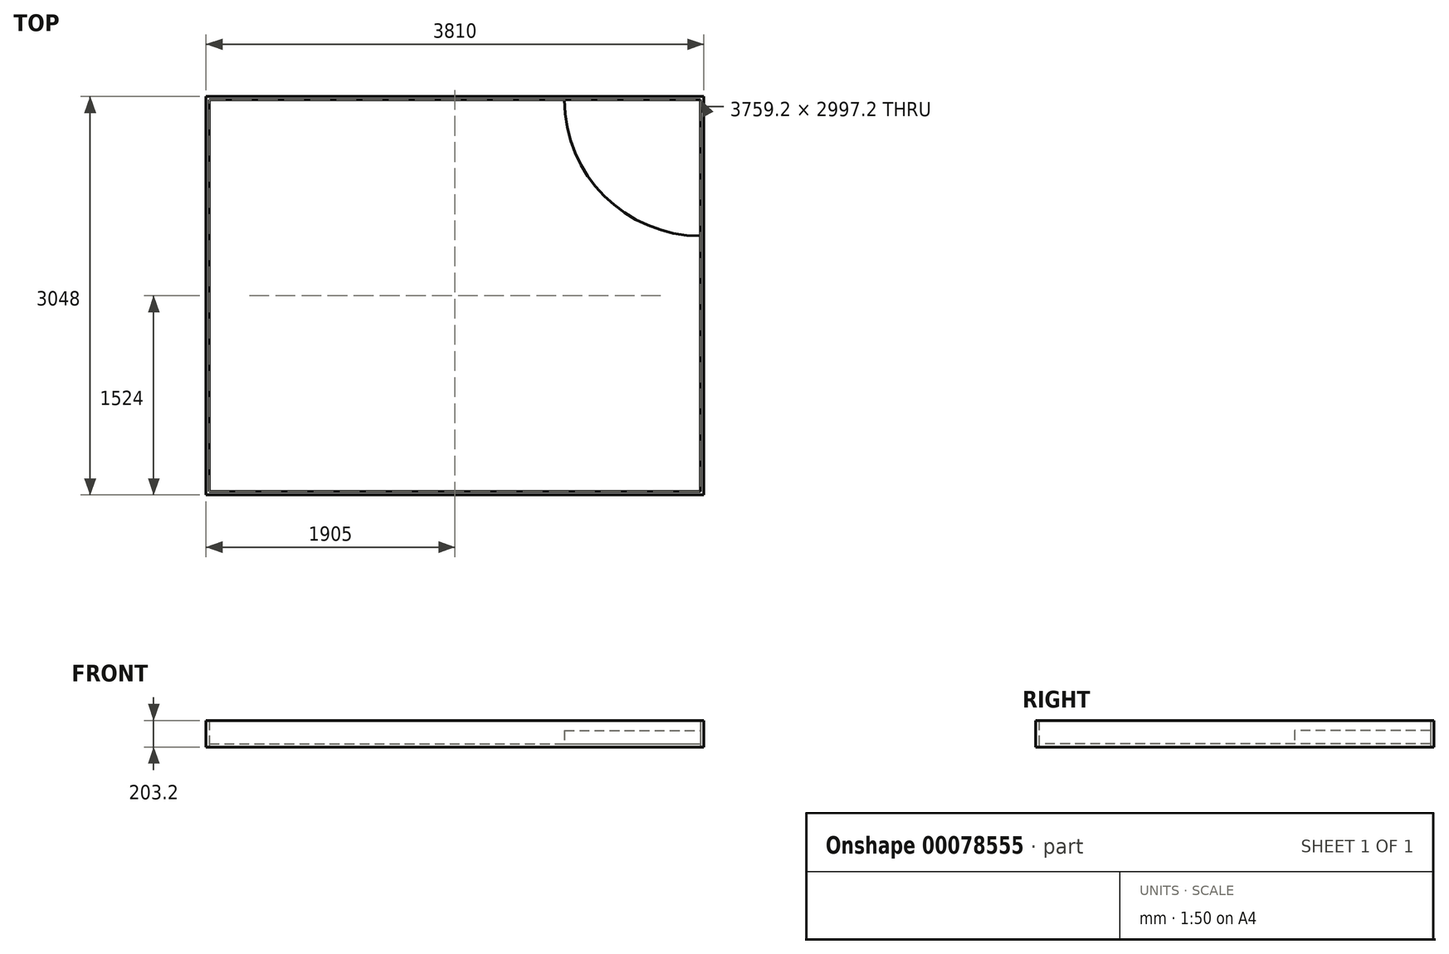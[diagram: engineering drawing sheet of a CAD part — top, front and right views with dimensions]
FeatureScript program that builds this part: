
annotation { "Feature Type Name" : "Feature", "Feature Type Description" : "" }
export const myFeature = defineFeature(function(context is Context, id is Id, definition is map)
    precondition{}
    {
        {
            var Q0;
            Q0=qCreatedBy(makeId("Top.planeOp"),FACE);
            var sketch = newSketch(context, id + "F0", { "sketchPlane" : qUnion([Q0])});
            skLineSegment(sketch, "E0.bottom", {"start": v(-1874.04, 1728.23) * mm, "end": v(1885.16, 1728.23) * mm});
            skLineSegment(sketch, "E0.top", {"start": v(-1874.04, -1268.97) * mm, "end": v(1885.16, -1268.97) * mm});
            skLineSegment(sketch, "E0.left", {"start": v(-1874.04, 1728.23) * mm, "end": v(-1874.04, -1268.97) * mm});
            skLineSegment(sketch, "E0.right", {"start": v(1885.16, 1728.23) * mm, "end": v(1885.16, -1268.97) * mm});
            skSolve(sketch);
        }
        {
            var Q0;
            Q0=makeQuery(id+"F0.imprint","IMPRINT",FACE,{"disambiguationData":[TD([[makeQuery(id+"F0.imprint","IMPRINT",EDGE,{"derivedFrom":sQuery(id+"F0.wireOp",EDGE,"E0.bottom")}),-1.0]])]});
            extrude(context, id + "F1", {"entities" : qUnion([Q0]), "depth" : 25.4 * mm});
        }
        {
            var Q0;
            Q0=makeQuery(id+"F1.opExtrude","CAP_FACE",FACE,{"disambiguationData":[OSD([sQuery(id+"F0.wireOp",EDGE,"E0.bottom"),sQuery(id+"F0.wireOp",EDGE,"E0.top"),sQuery(id+"F0.wireOp",EDGE,"E0.left"),sQuery(id+"F0.wireOp",EDGE,"E0.right")])],"isStart":true});
            var sketch = newSketch(context, id + "F2", { "sketchPlane" : qUnion([Q0])});
            skLineSegment(sketch, "E1.bottom", {"start": v(1910.56, -1753.63) * mm, "end": v(-1899.44, -1753.63) * mm});
            skLineSegment(sketch, "E1.top", {"start": v(1910.56, 1294.37) * mm, "end": v(-1899.44, 1294.37) * mm});
            skLineSegment(sketch, "E1.left", {"start": v(1910.56, -1753.63) * mm, "end": v(1910.56, 1294.37) * mm});
            skLineSegment(sketch, "E1.right", {"start": v(-1899.44, -1753.63) * mm, "end": v(-1899.44, 1294.37) * mm});
            skSolve(sketch);
        }
        {
            var Q0;
            Q0=makeQuery(id+"F2.imprint","IMPRINT",FACE,{"disambiguationData":[TD([[makeQuery(id+"F2.imprint","IMPRINT",EDGE,{"derivedFrom":sQuery(id+"F2.wireOp",EDGE,"E1.bottom")}),-1.0]])]});
            extrude(context, id + "F3", {"entities" : qUnion([Q0]), "oppositeDirection" : true, "depth" : 203.2 * mm});
        }
        {
            var Q0;
            Q0=makeQuery(id+"F1.opExtrude","CAP_FACE",FACE,{"disambiguationData":[OSD([sQuery(id+"F0.wireOp",EDGE,"E0.bottom"),sQuery(id+"F0.wireOp",EDGE,"E0.top"),sQuery(id+"F0.wireOp",EDGE,"E0.left"),sQuery(id+"F0.wireOp",EDGE,"E0.right")])],"isStart":false});
            var sketch = newSketch(context, id + "F4", { "sketchPlane" : qUnion([Q0])});
            skCircle(sketch, "E2", {"center": v(1885.16, 1728.23) * mm, "radius": 1041.4 * mm});
            skSolve(sketch);
        }
        {
            var Q0;
            {var subQ0=sQuery(id+"F4.wireOp",EDGE,"E2");var subQ1=makeQuery(id+"F1.opExtrude","CAP_EDGE",EDGE,{"disambiguationData":[OSD([sQuery(id+"F0.wireOp",EDGE,"E0.bottom")])],"isStart":false});var subQ2=makeQuery(id+"F4.imprint","INTERSECT",VERTEX,{"derivedFrom":[subQ1,subQ0]});Q0=makeQuery(id+"F4.imprint","IMPRINT",FACE,{"disambiguationData":[TD([[makeQuery(id+"F4.imprint","IMPRINT",EDGE,{"disambiguationData":[TD([[subQ2,-1.0]])],"derivedFrom":subQ0}),1.0]])]});}
            extrude(context, id + "F5", {"entities" : qUnion([Q0]), "depth" : 101.6 * mm});
        }
    });
